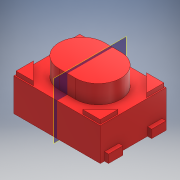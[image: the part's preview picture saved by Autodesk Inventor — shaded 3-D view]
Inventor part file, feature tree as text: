
AUTODESK INVENTOR PART (.ipt)
format: ipt  version: 2018 (Build 220112000, 112)  size: 187,904 bytes
history: native  units: mm
features: other x4, extrude x4, mirror x4, sketch x4
ambient origin geometry x8: Origin, YZ Plane, XZ Plane, XY Plane, X Axis, Y Axis, Z Axis, Center Point
bodies: Body1 (feature_tree), Body2 (feature_tree), Body3 (feature_tree), Body4 (feature_tree), Body5 (feature_tree), Body6 (feature_tree), Body7 (feature_tree)
feature tree (16):
  other  "ソリッド1"
  extrude  "押し出し1"  Depth=4.2mm
  extrude  "押し出し2"  Depth=3.2mm
  extrude  "押し出し3"  Depth=1.6mm TaperAngle=0.0deg
  mirror  "ミラー1"
  mirror  "ミラー2"
  extrude  "押し出し4"  Depth=2.2mm
  mirror  "ミラー3"
  mirror  "ミラー4"
  sketch  "スケッチ1"
  sketch  "スケッチ2"
  sketch  "スケッチ3"
  other  "作業平面1"
  other  "作業平面2"
  other  "作業平面3"
  sketch  "スケッチ4"
